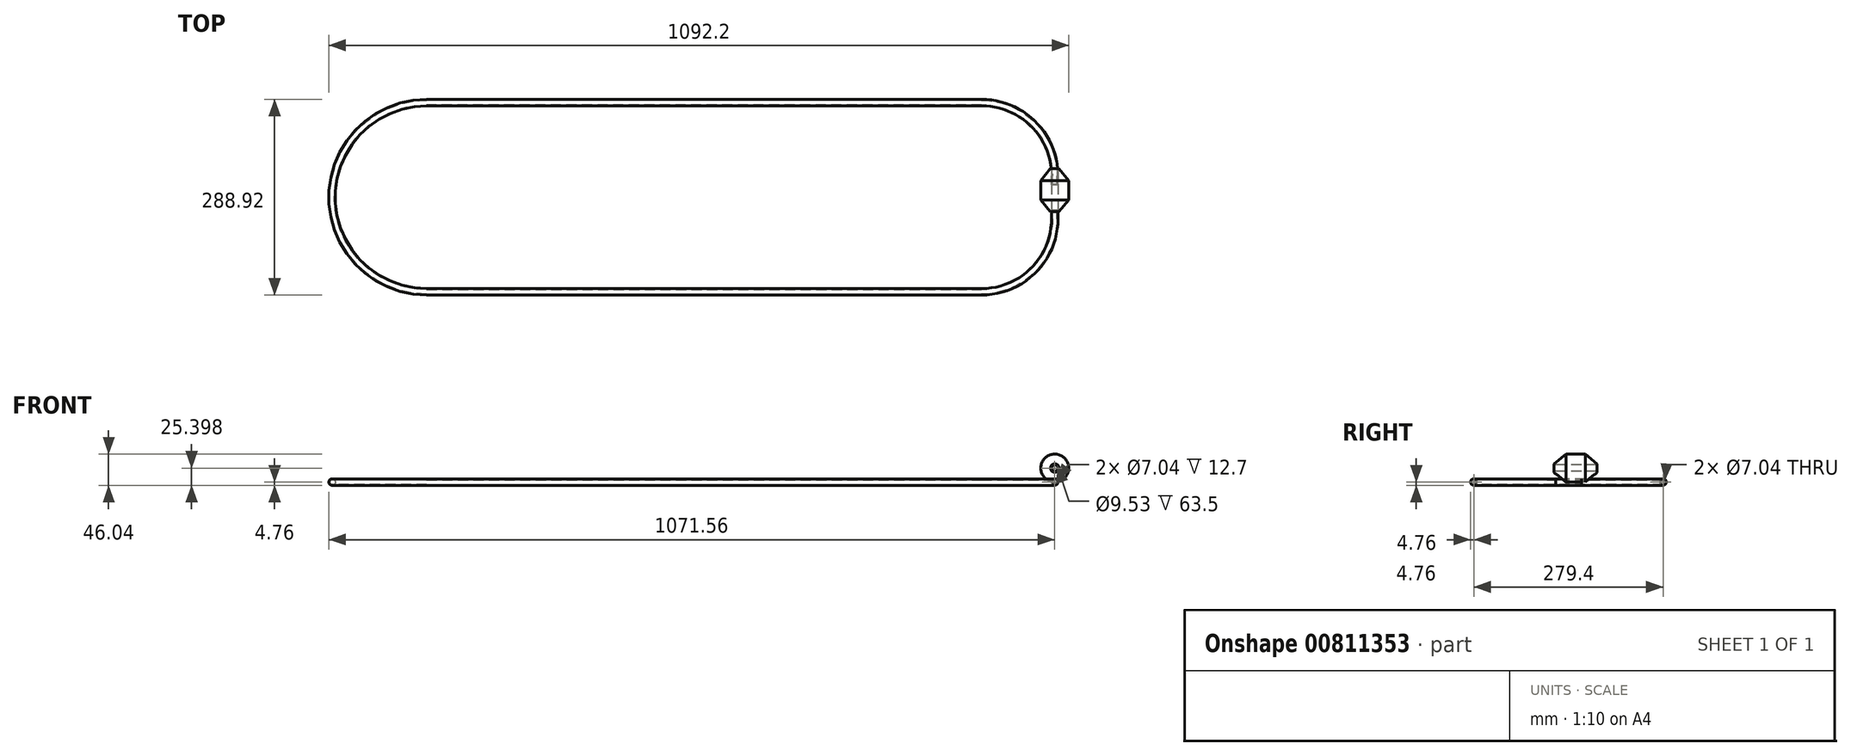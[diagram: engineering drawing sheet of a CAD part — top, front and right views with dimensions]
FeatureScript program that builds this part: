
annotation { "Feature Type Name" : "Feature", "Feature Type Description" : "" }
export const myFeature = defineFeature(function(context is Context, id is Id, definition is map)
    precondition{}
    {
        {
            var Q0;
            Q0=qCreatedBy(makeId("Top.planeOp"),FACE);
            var sketch = newSketch(context, id + "F0", { "sketchPlane" : qUnion([Q0])});
            skLineSegment(sketch, "E0.bottom", {"start": v(-107.95, 120.65) * mm, "end": v(-927.1, 120.65) * mm});
            skLineSegment(sketch, "E0.top", {"start": v(-107.95, -158.75) * mm, "end": v(-927.1, -158.75) * mm});
            skLineSegment(sketch, "E0.right", {"start": v(-533.4, 0) * mm, "end": v(-533.4, 0) * mm});
            skPoint(sketch, "E0.middle", {"position": v(-533.4, -19.05) * mm});
            skPoint(sketch, "E1.visualSharp", {"position": v(-1066.8, 120.65) * mm});
            skArc(sketch, "E1.filletArc", {"start": v(-927.1, 120.65) * mm, "mid": v(-1025.88, 79.73) * mm, "end": v(-1066.8, -19.05) * mm});
            skPoint(sketch, "E2.visualSharp", {"position": v(-1066.8, -158.75) * mm});
            skArc(sketch, "E2.filletArc", {"start": v(-1066.8, -19.05) * mm, "mid": v(-1025.88, -117.83) * mm, "end": v(-927.1, -158.75) * mm});
            skPoint(sketch, "E3.visualSharp", {"position": v(0, 139.7) * mm});
            skArc(sketch, "E3.filletArc", {"start": v(0, 12.7) * mm, "mid": v(-31.62, 89.03) * mm, "end": v(-107.95, 120.65) * mm});
            skPoint(sketch, "E4.visualSharp", {"position": v(0, -139.7) * mm});
            skArc(sketch, "E4.filletArc", {"start": v(-107.95, -158.75) * mm, "mid": v(-31.62, -127.13) * mm, "end": v(0, -50.8) * mm});
            skLineSegment(sketch, "E5", {"start": v(0, -50.8) * mm, "end": v(0, -38.1) * mm});
            skLineSegment(sketch, "E6", {"start": v(0, 12.7) * mm, "end": v(0, 0) * mm});
            skSolve(sketch);
        }
        {
            var Q0;
            Q0=qCreatedBy(makeId("Front.planeOp"),FACE);
            var sketch = newSketch(context, id + "F1", { "sketchPlane" : qUnion([Q0])});
            skCircle(sketch, "E7", {"center": v(0, 0) * mm, "radius": 4.76 * mm});
            skCircle(sketch, "E8", {"center": v(0, 0) * mm, "radius": 3.52 * mm});
            skSolve(sketch);
        }
        {
            var Q0;
            Q0=qCreatedBy(makeId("Right.planeOp"),FACE);
            var sketch = newSketch(context, id + "F2", { "sketchPlane" : qUnion([Q0])});
            skLineSegment(sketch, "E9", {"start": v(-40.34, 25.4) * mm, "end": v(-40.34, 26.99) * mm});
            skLineSegment(sketch, "E10", {"start": v(-40.34, 25.4) * mm, "end": v(23.16, 25.4) * mm});
            skLineSegment(sketch, "E11", {"start": v(23.16, 25.4) * mm, "end": v(23.16, 26.99) * mm});
            skLineSegment(sketch, "E12", {"start": v(23.16, 26.99) * mm, "end": v(5.7, 41.28) * mm});
            skLineSegment(sketch, "E13", {"start": v(5.7, 41.28) * mm, "end": v(-22.87, 41.28) * mm});
            skLineSegment(sketch, "E14", {"start": v(-22.87, 41.28) * mm, "end": v(-40.34, 26.99) * mm});
            skLineSegment(sketch, "E15", {"start": v(-40.34, 20.64) * mm, "end": v(23.16, 20.64) * mm});
            skLineSegment(sketch, "E16.0", {"start": v(-40.34, 0) * mm, "end": v(23.16, 0) * mm});
            skSolve(sketch);
        }
        {
            var Q0;
            Q0=makeQuery(id+"F2.imprint","IMPRINT",FACE,{"disambiguationData":[TD([[makeQuery(id+"F2.imprint","IMPRINT",EDGE,{"derivedFrom":sQuery(id+"F2.wireOp",EDGE,"E9")}),-1.0]])]});
            var Q1;
            Q1=sQuery(id+"F2.wireOp",EDGE,"E15");
            revolve(context, id + "F3", {"surfaceOperationType" : NewSurfaceOperationType.NEW, "entities" : qUnion([Q0]), "axis" : qUnion([Q1]), "revolveType" : RevolveType.FULL});
        }
        {
            var Q0;
            Q0=makeQuery(id+"F1.imprint","IMPRINT",FACE,{"disambiguationData":[TD([[makeQuery(id+"F1.imprint","IMPRINT",EDGE,{"derivedFrom":sQuery(id+"F1.wireOp",EDGE,"E7")}),1.0]])]});
            var Q1;
            Q1=sQuery(id+"F0.wireOp",EDGE,"E6");
            var Q2;
            Q2=sQuery(id+"F0.wireOp",EDGE,"E3.filletArc");
            var Q3;
            Q3=sQuery(id+"F0.wireOp",EDGE,"E0.bottom");
            var Q4;
            Q4=sQuery(id+"F0.wireOp",EDGE,"E1.filletArc");
            var Q5;
            Q5=sQuery(id+"F0.wireOp",EDGE,"E2.filletArc");
            var Q6;
            Q6=sQuery(id+"F0.wireOp",EDGE,"E0.top");
            var Q7;
            Q7=sQuery(id+"F0.wireOp",EDGE,"E4.filletArc");
            var Q8;
            Q8=sQuery(id+"F0.wireOp",EDGE,"E5");
            sweep(context, id + "F4", {"profiles" : qUnion([Q0]), "path" : qUnion([Q1, Q2, Q3, Q4, Q5, Q6, Q7, Q8])});
        }
    });
